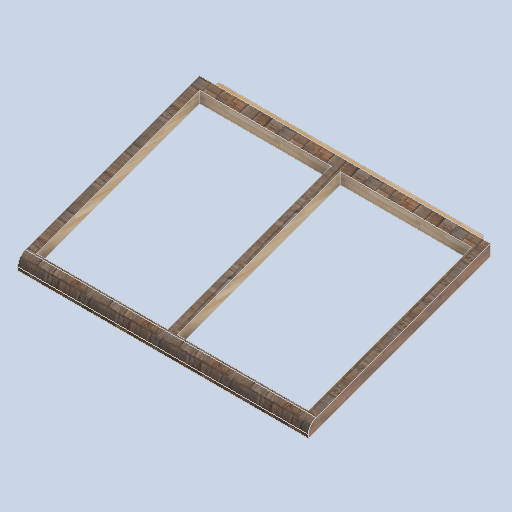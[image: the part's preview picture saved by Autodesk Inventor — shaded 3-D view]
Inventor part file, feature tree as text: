
AUTODESK INVENTOR PART (.ipt)
format: ipt  version: 2024.2 (Build 282272000, 272)  size: 245,760 bytes
history: native  units: mm
features: sketch x6, extrude x4, plane x2, projected_geometry x2, fillet x1
ambient origin geometry x8: Origin, YZ Plane, XZ Plane, XY Plane, X Axis, Y Axis, Z Axis, Center Point
bodies: Solid1 (feature_tree)
feature tree (15):
  extrude  "Extrusion1"  Depth=50.0mm TaperAngle=0.0deg
  plane  "Work Plane1"
  plane  "Work Plane2"
  extrude  "Extrusion2"  Depth=2500.0mm
  extrude  "Extrusion3"  Depth=150.0mm
  sketch  "Sketch4"  dims[d8=3752.0mm d9=0.0mm d10=0.0mm d11=0.0mm]
  sketch  "Sketch5"  dims[d12=400.0mm]
  fillet  "Fillet1"  Radius=3752.111457mm
  extrude  "Extrusion5"  TaperAngle=0.0deg  [1 undecoded]
  sketch  "Sketch6"  dims[d13=10.0mm d14=20.0mm d15=400.0mm d16=20.0mm d17=400.0mm d18=20.0mm d19=400.0mm d20=20.0mm d21=400.0mm d22=20.0mm d23=120.0mm d24=120.0mm d25=120.0mm d26=120.0mm d29=150.0mm d32=0.0mm d33=0.0mm]
  sketch  "Sketch1"  dims[d0=150.0mm d1=50.0mm d2=0.0mm]
  sketch  "Sketch2"  dims[d3=0.0mm d4=2500.0mm]
  sketch  "Sketch3"  dims[d5=12.217305mm d6=150.0mm d7=3752.111457mm]
  projected_geometry  "Projected Loop1"
  projected_geometry  "Projected Loop2"
note: 1 required parameter value undecoded (feature->parameter linkage not recoverable at this tier; creation-order binding heuristic only, values carry confidence <= 0.55)
